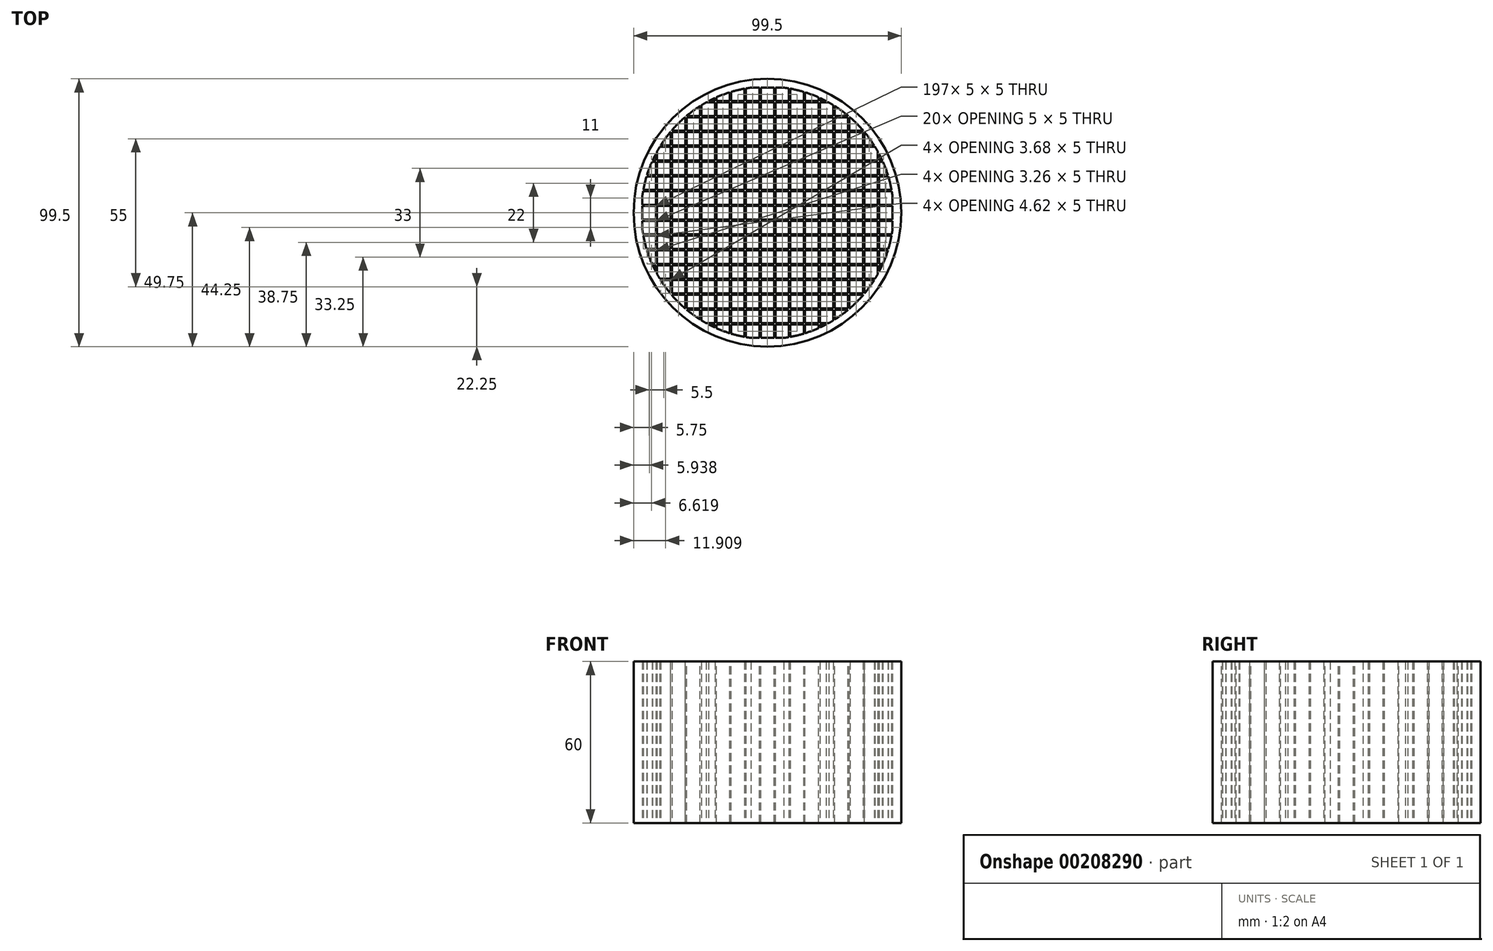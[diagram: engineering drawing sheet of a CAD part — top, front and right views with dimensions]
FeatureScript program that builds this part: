
annotation { "Feature Type Name" : "Feature", "Feature Type Description" : "" }
export const myFeature = defineFeature(function(context is Context, id is Id, definition is map)
    precondition{}
    {
        {
            var Q0;
            Q0=qCreatedBy(makeId("Top.planeOp"),FACE);
            var sketch = newSketch(context, id + "F0", { "sketchPlane" : qUnion([Q0])});
            skCircle(sketch, "E0", {"center": v(0, 0) * mm, "radius": 46.9 * mm});
            skCircle(sketch, "E1", {"center": v(0, 0) * mm, "radius": 49.75 * mm});
            skSolve(sketch);
        }
        {
            var Q0;
            Q0 = qSketchRegion(id + "F0", true);
            extrude(context, id + "F1", {"entities" : qUnion([Q0]), "depth" : 60 * mm, "offsetDistance" : 25 * mm});
        }
        {
            var Q0;
            Q0=qCreatedBy(makeId("Top.planeOp"),FACE);
            var sketch = newSketch(context, id + "F2", { "sketchPlane" : qUnion([Q0])});
            skCircle(sketch, "E2.0", {"center": v(0, 0) * mm, "radius": 46.9 * mm});
            skLineSegment(sketch, "E3", {"start": v(-2.5, 46.83) * mm, "end": v(-2.5, -46.83) * mm});
            skLineSegment(sketch, "E4", {"start": v(-3, 46.8) * mm, "end": v(-3, -46.8) * mm});
            skLineSegment(sketch, "E5", {"start": v(-8, 46.21) * mm, "end": v(-8, -46.21) * mm});
            skLineSegment(sketch, "E6", {"start": v(-8.5, -46.12) * mm, "end": v(-8.5, 46.12) * mm});
            skLineSegment(sketch, "E7", {"start": v(-13.5, 44.92) * mm, "end": v(-13.5, -44.92) * mm});
            skLineSegment(sketch, "E8", {"start": v(-19, 42.88) * mm, "end": v(-19, -42.88) * mm});
            skLineSegment(sketch, "E9", {"start": v(-14, 44.76) * mm, "end": v(-14, -44.76) * mm});
            skLineSegment(sketch, "E10", {"start": v(-19.5, 42.65) * mm, "end": v(-19.5, -42.65) * mm});
            skLineSegment(sketch, "E11", {"start": v(-24.5, 40) * mm, "end": v(-24.5, -40) * mm});
            skLineSegment(sketch, "E12", {"start": v(-25, 39.68) * mm, "end": v(-25, -39.68) * mm});
            skLineSegment(sketch, "E13", {"start": v(-30.5, 35.63) * mm, "end": v(-30.5, -35.63) * mm});
            skLineSegment(sketch, "E14", {"start": v(-30, 36.05) * mm, "end": v(-30, -36.05) * mm});
            skLineSegment(sketch, "E15", {"start": v(-35.5, 30.65) * mm, "end": v(-35.5, -30.65) * mm});
            skLineSegment(sketch, "E16", {"start": v(-36, 30.06) * mm, "end": v(-36, -30.06) * mm});
            skLineSegment(sketch, "E17", {"start": v(-41, 22.77) * mm, "end": v(-41, -22.77) * mm});
            skLineSegment(sketch, "E18", {"start": v(-41.5, 21.85) * mm, "end": v(-41.5, -21.85) * mm});
            skLineSegment(sketch, "E19", {"start": v(-46.5, 6.11) * mm, "end": v(-46.5, -6.11) * mm});
            skLineSegment(sketch, "E20.MirrorCS", {"start": v(2.5, 46.83) * mm, "end": v(2.5, -46.83) * mm});
            skLineSegment(sketch, "E21.MirrorCS", {"start": v(19.5, 42.65) * mm, "end": v(19.5, -42.65) * mm});
            skLineSegment(sketch, "E22.MirrorCS", {"start": v(30.5, 35.63) * mm, "end": v(30.5, -35.63) * mm});
            skLineSegment(sketch, "E23.MirrorCS", {"start": v(36, 30.06) * mm, "end": v(36, -30.06) * mm});
            skLineSegment(sketch, "E24.MirrorCS", {"start": v(30, 36.05) * mm, "end": v(30, -36.05) * mm});
            skLineSegment(sketch, "E25.MirrorCS", {"start": v(25, 39.68) * mm, "end": v(25, -39.68) * mm});
            skLineSegment(sketch, "E26.MirrorCS", {"start": v(3, 46.8) * mm, "end": v(3, -46.8) * mm});
            skLineSegment(sketch, "E27.MirrorCS", {"start": v(41, 22.77) * mm, "end": v(41, -22.77) * mm});
            skLineSegment(sketch, "E28.MirrorCS", {"start": v(14, 44.76) * mm, "end": v(14, -44.76) * mm});
            skLineSegment(sketch, "E29.MirrorCS", {"start": v(35.5, 30.65) * mm, "end": v(35.5, -30.65) * mm});
            skLineSegment(sketch, "E30.MirrorCS", {"start": v(8.5, -46.12) * mm, "end": v(8.5, 46.12) * mm});
            skLineSegment(sketch, "E31.MirrorCS", {"start": v(46.5, 6.11) * mm, "end": v(46.5, -6.11) * mm});
            skLineSegment(sketch, "E32.MirrorCS", {"start": v(19, 42.88) * mm, "end": v(19, -42.88) * mm});
            skLineSegment(sketch, "E33.MirrorCS", {"start": v(13.5, 44.92) * mm, "end": v(13.5, -44.92) * mm});
            skLineSegment(sketch, "E34.MirrorCS", {"start": v(41.5, 21.85) * mm, "end": v(41.5, -21.85) * mm});
            skLineSegment(sketch, "E35.MirrorCS", {"start": v(24.5, 40) * mm, "end": v(24.5, -40) * mm});
            skLineSegment(sketch, "E36.MirrorCS", {"start": v(8, 46.21) * mm, "end": v(8, -46.21) * mm});
            skSolve(sketch);
        }
        {
            var Q0;
            {var subQ0=sQuery(id+"F2.wireOp",EDGE,"E13");Q0=makeQuery(id+"F2.imprint","IMPRINT",FACE,{"disambiguationData":[TD([[makeQuery(id+"F2.imprint","IMPRINT",EDGE,{"derivedFrom":subQ0}),1.0]])]});}
            var Q1;
            {var subQ0=sQuery(id+"F2.wireOp",EDGE,"E15");Q1=makeQuery(id+"F2.imprint","IMPRINT",FACE,{"disambiguationData":[TD([[makeQuery(id+"F2.imprint","IMPRINT",EDGE,{"derivedFrom":subQ0}),-1.0]])]});}
            var Q2;
            {var subQ0=sQuery(id+"F2.wireOp",EDGE,"E19");Q2=makeQuery(id+"F2.imprint","IMPRINT",FACE,{"disambiguationData":[TD([[makeQuery(id+"F2.imprint","IMPRINT",EDGE,{"derivedFrom":subQ0}),-1.0]])]});}
            var Q3;
            {var subQ0=sQuery(id+"F2.wireOp",EDGE,"E17");Q3=makeQuery(id+"F2.imprint","IMPRINT",FACE,{"disambiguationData":[TD([[makeQuery(id+"F2.imprint","IMPRINT",EDGE,{"derivedFrom":subQ0}),-1.0]])]});}
            var Q4;
            {var subQ0=sQuery(id+"F2.wireOp",EDGE,"E11");Q4=makeQuery(id+"F2.imprint","IMPRINT",FACE,{"disambiguationData":[TD([[makeQuery(id+"F2.imprint","IMPRINT",EDGE,{"derivedFrom":subQ0}),-1.0]])]});}
            var Q5;
            {var subQ0=sQuery(id+"F2.wireOp",EDGE,"E8");Q5=makeQuery(id+"F2.imprint","IMPRINT",FACE,{"disambiguationData":[TD([[makeQuery(id+"F2.imprint","IMPRINT",EDGE,{"derivedFrom":subQ0}),-1.0]])]});}
            var Q6;
            {var subQ0=sQuery(id+"F2.wireOp",EDGE,"E7");Q6=makeQuery(id+"F2.imprint","IMPRINT",FACE,{"disambiguationData":[TD([[makeQuery(id+"F2.imprint","IMPRINT",EDGE,{"derivedFrom":subQ0}),-1.0]])]});}
            var Q7;
            {var subQ0=sQuery(id+"F2.wireOp",EDGE,"E5");Q7=makeQuery(id+"F2.imprint","IMPRINT",FACE,{"disambiguationData":[TD([[makeQuery(id+"F2.imprint","IMPRINT",EDGE,{"derivedFrom":subQ0}),-1.0]])]});}
            var Q8;
            {var subQ0=sQuery(id+"F2.wireOp",EDGE,"E3");Q8=makeQuery(id+"F2.imprint","IMPRINT",FACE,{"disambiguationData":[TD([[makeQuery(id+"F2.imprint","IMPRINT",EDGE,{"derivedFrom":subQ0}),-1.0]])]});}
            var Q9;
            {var subQ0=sQuery(id+"F2.wireOp",EDGE,"E20.MirrorCS");Q9=makeQuery(id+"F2.imprint","IMPRINT",FACE,{"disambiguationData":[TD([[makeQuery(id+"F2.imprint","IMPRINT",EDGE,{"derivedFrom":subQ0}),1.0]])]});}
            var Q10;
            {var subQ0=sQuery(id+"F2.wireOp",EDGE,"E30.MirrorCS");Q10=makeQuery(id+"F2.imprint","IMPRINT",FACE,{"disambiguationData":[TD([[makeQuery(id+"F2.imprint","IMPRINT",EDGE,{"derivedFrom":subQ0}),1.0]])]});}
            var Q11;
            {var subQ0=sQuery(id+"F2.wireOp",EDGE,"E28.MirrorCS");Q11=makeQuery(id+"F2.imprint","IMPRINT",FACE,{"disambiguationData":[TD([[makeQuery(id+"F2.imprint","IMPRINT",EDGE,{"derivedFrom":subQ0}),-1.0]])]});}
            var Q12;
            {var subQ0=sQuery(id+"F2.wireOp",EDGE,"E21.MirrorCS");Q12=makeQuery(id+"F2.imprint","IMPRINT",FACE,{"disambiguationData":[TD([[makeQuery(id+"F2.imprint","IMPRINT",EDGE,{"derivedFrom":subQ0}),-1.0]])]});}
            var Q13;
            {var subQ0=sQuery(id+"F2.wireOp",EDGE,"E25.MirrorCS");Q13=makeQuery(id+"F2.imprint","IMPRINT",FACE,{"disambiguationData":[TD([[makeQuery(id+"F2.imprint","IMPRINT",EDGE,{"derivedFrom":subQ0}),-1.0]])]});}
            var Q14;
            {var subQ0=sQuery(id+"F2.wireOp",EDGE,"E22.MirrorCS");Q14=makeQuery(id+"F2.imprint","IMPRINT",FACE,{"disambiguationData":[TD([[makeQuery(id+"F2.imprint","IMPRINT",EDGE,{"derivedFrom":subQ0}),-1.0]])]});}
            var Q15;
            {var subQ0=sQuery(id+"F2.wireOp",EDGE,"E23.MirrorCS");Q15=makeQuery(id+"F2.imprint","IMPRINT",FACE,{"disambiguationData":[TD([[makeQuery(id+"F2.imprint","IMPRINT",EDGE,{"derivedFrom":subQ0}),-1.0]])]});}
            var Q16;
            {var subQ0=sQuery(id+"F2.wireOp",EDGE,"E27.MirrorCS");Q16=makeQuery(id+"F2.imprint","IMPRINT",FACE,{"disambiguationData":[TD([[makeQuery(id+"F2.imprint","IMPRINT",EDGE,{"derivedFrom":subQ0}),1.0]])]});}
            var Q17;
            {var subQ0=sQuery(id+"F2.wireOp",EDGE,"E31.MirrorCS");Q17=makeQuery(id+"F2.imprint","IMPRINT",FACE,{"disambiguationData":[TD([[makeQuery(id+"F2.imprint","IMPRINT",EDGE,{"derivedFrom":subQ0}),1.0]])]});}
            extrude(context, id + "F3", {"entities" : qUnion([Q0, Q1, Q2, Q3, Q4, Q5, Q6, Q7, Q8, Q9, Q10, Q11, Q12, Q13, Q14, Q15, Q16, Q17]), "operationType" : NewBodyOperationType.ADD, "depth" : 60 * mm, "offsetDistance" : 25 * mm});
        }
        {
            var Q0;
            Q0=qCreatedBy(makeId("Top.planeOp"),FACE);
            var sketch = newSketch(context, id + "F4", { "sketchPlane" : qUnion([Q0])});
            skCircle(sketch, "E37", {"center": v(0, 0) * mm, "radius": 47 * mm});
            skLineSegment(sketch, "E38", {"start": v(-46.93, 2.5) * mm, "end": v(46.93, 2.5) * mm});
            skLineSegment(sketch, "E39", {"start": v(-46.31, 8) * mm, "end": v(46.31, 8) * mm});
            skLineSegment(sketch, "E40", {"start": v(-46.22, 8.5) * mm, "end": v(46.22, 8.5) * mm});
            skLineSegment(sketch, "E41", {"start": v(-45.02, 13.5) * mm, "end": v(45.02, 13.5) * mm});
            skLineSegment(sketch, "E42", {"start": v(-44.87, 14) * mm, "end": v(44.87, 14) * mm});
            skLineSegment(sketch, "E43", {"start": v(-40.1, 24.5) * mm, "end": v(40.1, 24.5) * mm});
            skLineSegment(sketch, "E44", {"start": v(-39.8, 25) * mm, "end": v(39.8, 25) * mm});
            skLineSegment(sketch, "E45", {"start": v(-42.99, 19) * mm, "end": v(42.99, 19) * mm});
            skLineSegment(sketch, "E46", {"start": v(-42.76, 19.5) * mm, "end": v(42.76, 19.5) * mm});
            skLineSegment(sketch, "E47", {"start": v(-36.18, 30) * mm, "end": v(36.18, 30) * mm});
            skLineSegment(sketch, "E48", {"start": v(-46.9, 3) * mm, "end": v(46.9, 3) * mm});
            skLineSegment(sketch, "E49", {"start": v(-35.76, 30.5) * mm, "end": v(35.76, 30.5) * mm});
            skLineSegment(sketch, "E50", {"start": v(-30.8, 35.5) * mm, "end": v(30.8, 35.5) * mm});
            skLineSegment(sketch, "E51", {"start": v(-30.22, 36) * mm, "end": v(30.22, 36) * mm});
            skLineSegment(sketch, "E52", {"start": v(-22.98, 41) * mm, "end": v(22.98, 41) * mm});
            skLineSegment(sketch, "E53", {"start": v(-22.06, 41.5) * mm, "end": v(22.06, 41.5) * mm});
            skLineSegment(sketch, "E54", {"start": v(-6.84, 46.5) * mm, "end": v(6.84, 46.5) * mm});
            skLineSegment(sketch, "E55.MirrorCS", {"start": v(-46.31, -8) * mm, "end": v(46.31, -8) * mm});
            skLineSegment(sketch, "E56.MirrorCS", {"start": v(-36.18, -30) * mm, "end": v(36.18, -30) * mm});
            skLineSegment(sketch, "E57.MirrorCS", {"start": v(-22.06, -41.5) * mm, "end": v(22.06, -41.5) * mm});
            skLineSegment(sketch, "E58.MirrorCS", {"start": v(-42.99, -19) * mm, "end": v(42.99, -19) * mm});
            skLineSegment(sketch, "E59.MirrorCS", {"start": v(-42.76, -19.5) * mm, "end": v(42.76, -19.5) * mm});
            skLineSegment(sketch, "E60.MirrorCS", {"start": v(-30.22, -36) * mm, "end": v(30.22, -36) * mm});
            skLineSegment(sketch, "E61.MirrorCS", {"start": v(-22.98, -41) * mm, "end": v(22.98, -41) * mm});
            skLineSegment(sketch, "E62.MirrorCS", {"start": v(-35.76, -30.5) * mm, "end": v(35.76, -30.5) * mm});
            skLineSegment(sketch, "E63.MirrorCS", {"start": v(-45.02, -13.5) * mm, "end": v(45.02, -13.5) * mm});
            skLineSegment(sketch, "E64.MirrorCS", {"start": v(-46.9, -3) * mm, "end": v(46.9, -3) * mm});
            skLineSegment(sketch, "E65.MirrorCS", {"start": v(-46.22, -8.5) * mm, "end": v(46.22, -8.5) * mm});
            skLineSegment(sketch, "E66.MirrorCS", {"start": v(-46.93, -2.5) * mm, "end": v(46.93, -2.5) * mm});
            skLineSegment(sketch, "E67.MirrorCS", {"start": v(-6.84, -46.5) * mm, "end": v(6.84, -46.5) * mm});
            skLineSegment(sketch, "E68.MirrorCS", {"start": v(-44.87, -14) * mm, "end": v(44.87, -14) * mm});
            skLineSegment(sketch, "E69.MirrorCS", {"start": v(-40.1, -24.5) * mm, "end": v(40.1, -24.5) * mm});
            skLineSegment(sketch, "E70.MirrorCS", {"start": v(-30.8, -35.5) * mm, "end": v(30.8, -35.5) * mm});
            skLineSegment(sketch, "E71.MirrorCS", {"start": v(-39.8, -25) * mm, "end": v(39.8, -25) * mm});
            skSolve(sketch);
        }
        {
            var Q0;
            {var subQ0=sQuery(id+"F4.wireOp",EDGE,"E54");Q0=makeQuery(id+"F4.imprint","IMPRINT",FACE,{"disambiguationData":[TD([[makeQuery(id+"F4.imprint","IMPRINT",EDGE,{"derivedFrom":subQ0}),1.0]])]});}
            var Q1;
            {var subQ0=sQuery(id+"F4.wireOp",EDGE,"E52");Q1=makeQuery(id+"F4.imprint","IMPRINT",FACE,{"disambiguationData":[TD([[makeQuery(id+"F4.imprint","IMPRINT",EDGE,{"derivedFrom":subQ0}),1.0]])]});}
            var Q2;
            {var subQ0=sQuery(id+"F4.wireOp",EDGE,"E50");Q2=makeQuery(id+"F4.imprint","IMPRINT",FACE,{"disambiguationData":[TD([[makeQuery(id+"F4.imprint","IMPRINT",EDGE,{"derivedFrom":subQ0}),1.0]])]});}
            var Q3;
            {var subQ0=sQuery(id+"F4.wireOp",EDGE,"E47");Q3=makeQuery(id+"F4.imprint","IMPRINT",FACE,{"disambiguationData":[TD([[makeQuery(id+"F4.imprint","IMPRINT",EDGE,{"derivedFrom":subQ0}),1.0]])]});}
            var Q4;
            {var subQ0=sQuery(id+"F4.wireOp",EDGE,"E43");Q4=makeQuery(id+"F4.imprint","IMPRINT",FACE,{"disambiguationData":[TD([[makeQuery(id+"F4.imprint","IMPRINT",EDGE,{"derivedFrom":subQ0}),1.0]])]});}
            var Q5;
            {var subQ0=sQuery(id+"F4.wireOp",EDGE,"E45");Q5=makeQuery(id+"F4.imprint","IMPRINT",FACE,{"disambiguationData":[TD([[makeQuery(id+"F4.imprint","IMPRINT",EDGE,{"derivedFrom":subQ0}),1.0]])]});}
            var Q6;
            {var subQ0=sQuery(id+"F4.wireOp",EDGE,"E67.MirrorCS");Q6=makeQuery(id+"F4.imprint","IMPRINT",FACE,{"disambiguationData":[TD([[makeQuery(id+"F4.imprint","IMPRINT",EDGE,{"derivedFrom":subQ0}),-1.0]])]});}
            var Q7;
            {var subQ0=sQuery(id+"F4.wireOp",EDGE,"E57.MirrorCS");Q7=makeQuery(id+"F4.imprint","IMPRINT",FACE,{"disambiguationData":[TD([[makeQuery(id+"F4.imprint","IMPRINT",EDGE,{"derivedFrom":subQ0}),1.0]])]});}
            var Q8;
            {var subQ0=sQuery(id+"F4.wireOp",EDGE,"E60.MirrorCS");Q8=makeQuery(id+"F4.imprint","IMPRINT",FACE,{"disambiguationData":[TD([[makeQuery(id+"F4.imprint","IMPRINT",EDGE,{"derivedFrom":subQ0}),1.0]])]});}
            var Q9;
            {var subQ0=sQuery(id+"F4.wireOp",EDGE,"E56.MirrorCS");Q9=makeQuery(id+"F4.imprint","IMPRINT",FACE,{"disambiguationData":[TD([[makeQuery(id+"F4.imprint","IMPRINT",EDGE,{"derivedFrom":subQ0}),-1.0]])]});}
            var Q10;
            {var subQ0=sQuery(id+"F4.wireOp",EDGE,"E69.MirrorCS");Q10=makeQuery(id+"F4.imprint","IMPRINT",FACE,{"disambiguationData":[TD([[makeQuery(id+"F4.imprint","IMPRINT",EDGE,{"derivedFrom":subQ0}),-1.0]])]});}
            var Q11;
            {var subQ0=sQuery(id+"F4.wireOp",EDGE,"E58.MirrorCS");Q11=makeQuery(id+"F4.imprint","IMPRINT",FACE,{"disambiguationData":[TD([[makeQuery(id+"F4.imprint","IMPRINT",EDGE,{"derivedFrom":subQ0}),-1.0]])]});}
            var Q12;
            {var subQ0=sQuery(id+"F4.wireOp",EDGE,"E63.MirrorCS");Q12=makeQuery(id+"F4.imprint","IMPRINT",FACE,{"disambiguationData":[TD([[makeQuery(id+"F4.imprint","IMPRINT",EDGE,{"derivedFrom":subQ0}),-1.0]])]});}
            var Q13;
            {var subQ0=sQuery(id+"F4.wireOp",EDGE,"E55.MirrorCS");Q13=makeQuery(id+"F4.imprint","IMPRINT",FACE,{"disambiguationData":[TD([[makeQuery(id+"F4.imprint","IMPRINT",EDGE,{"derivedFrom":subQ0}),-1.0]])]});}
            var Q14;
            {var subQ0=sQuery(id+"F4.wireOp",EDGE,"E64.MirrorCS");Q14=makeQuery(id+"F4.imprint","IMPRINT",FACE,{"disambiguationData":[TD([[makeQuery(id+"F4.imprint","IMPRINT",EDGE,{"derivedFrom":subQ0}),1.0]])]});}
            var Q15;
            {var subQ0=sQuery(id+"F4.wireOp",EDGE,"E41");Q15=makeQuery(id+"F4.imprint","IMPRINT",FACE,{"disambiguationData":[TD([[makeQuery(id+"F4.imprint","IMPRINT",EDGE,{"derivedFrom":subQ0}),1.0]])]});}
            var Q16;
            {var subQ0=sQuery(id+"F4.wireOp",EDGE,"E39");Q16=makeQuery(id+"F4.imprint","IMPRINT",FACE,{"disambiguationData":[TD([[makeQuery(id+"F4.imprint","IMPRINT",EDGE,{"derivedFrom":subQ0}),1.0]])]});}
            var Q17;
            {var subQ0=sQuery(id+"F4.wireOp",EDGE,"E38");Q17=makeQuery(id+"F4.imprint","IMPRINT",FACE,{"disambiguationData":[TD([[makeQuery(id+"F4.imprint","IMPRINT",EDGE,{"derivedFrom":subQ0}),1.0]])]});}
            extrude(context, id + "F5", {"entities" : qUnion([Q0, Q1, Q2, Q3, Q4, Q5, Q6, Q7, Q8, Q9, Q10, Q11, Q12, Q13, Q14, Q15, Q16, Q17]), "operationType" : NewBodyOperationType.ADD, "depth" : 60 * mm, "offsetDistance" : 25 * mm});
        }
    });
